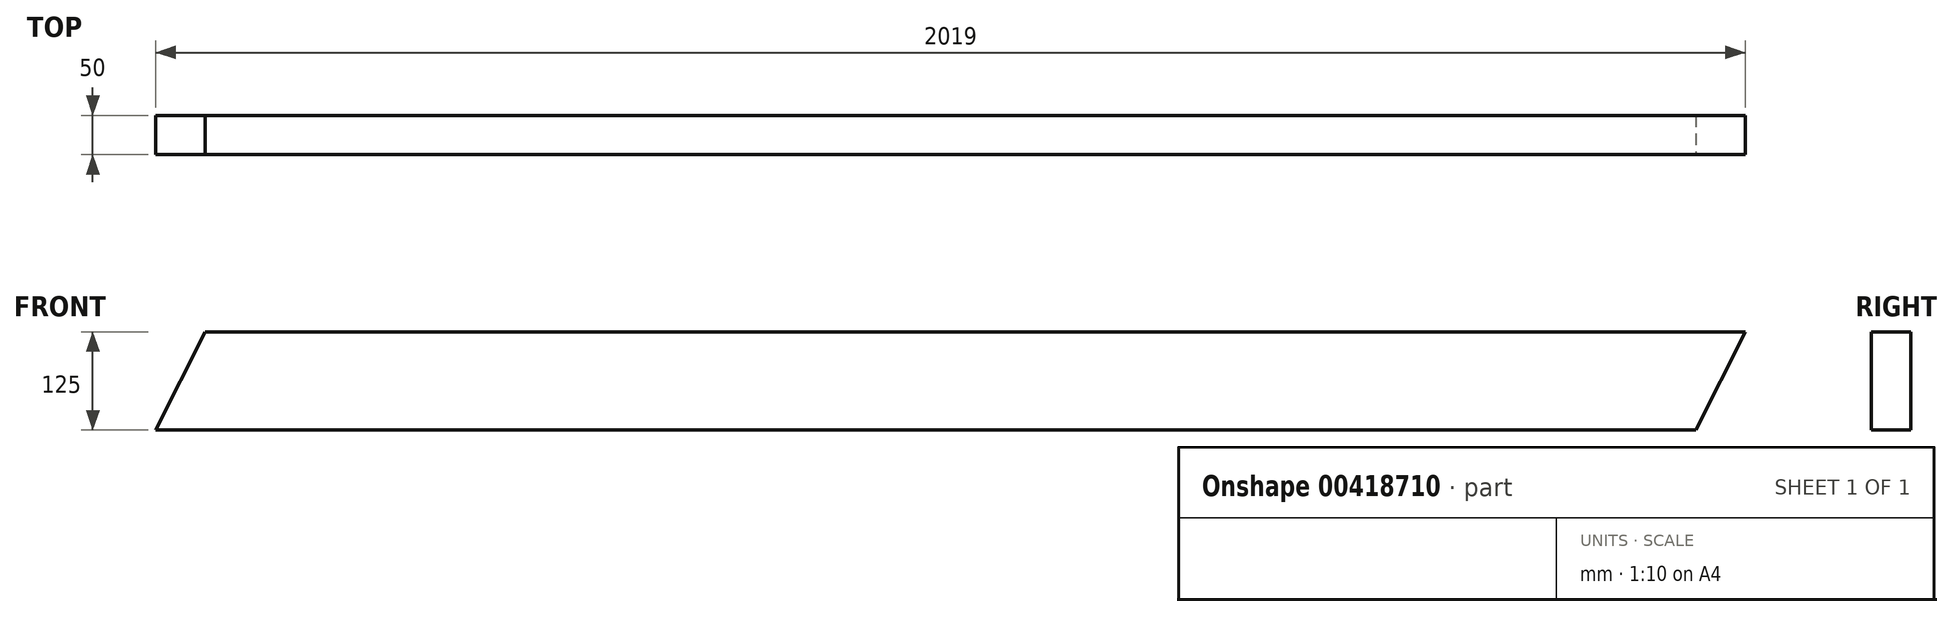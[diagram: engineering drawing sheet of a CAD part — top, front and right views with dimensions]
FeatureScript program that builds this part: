
annotation { "Feature Type Name" : "Feature", "Feature Type Description" : "" }
export const myFeature = defineFeature(function(context is Context, id is Id, definition is map)
    precondition{}
    {
        {
            var Q0;
            Q0=qCreatedBy(makeId("Right.planeOp"),FACE);
            var sketch = newSketch(context, id + "F0", { "sketchPlane" : qUnion([Q0])});
            skLineSegment(sketch, "E0.bottom", {"start": v(25, 62.5) * mm, "end": v(-25, 62.5) * mm});
            skLineSegment(sketch, "E0.top", {"start": v(25, -62.5) * mm, "end": v(-25, -62.5) * mm});
            skLineSegment(sketch, "E0.left", {"start": v(25, 62.5) * mm, "end": v(25, -62.5) * mm});
            skLineSegment(sketch, "E0.right", {"start": v(-25, 62.5) * mm, "end": v(-25, -62.5) * mm});
            skPoint(sketch, "E0.middle", {"position": v(0, 0) * mm});
            skSolve(sketch);
        }
        {
            var Q0;
            Q0 = qSketchRegion(id + "F0", true);
            extrude(context, id + "F1", {"entities" : qUnion([Q0]), "oppositeDirection" : true, "depth" : (2000 + 19) * mm});
        }
        {
            var Q0;
            Q0=qCreatedBy(makeId("Front.planeOp"),FACE);
            var sketch = newSketch(context, id + "F2", { "sketchPlane" : qUnion([Q0])});
            skLineSegment(sketch, "E1", {"start": v(0, 62.5) * mm, "end": v(0, -62.5) * mm});
            skLineSegment(sketch, "E2", {"start": v(0, -62.5) * mm, "end": v(-62.5, -62.5) * mm});
            skLineSegment(sketch, "E3", {"start": v(-62.5, -62.5) * mm, "end": v(0, 62.5) * mm});
            skLineSegment(sketch, "E4", {"start": v(-2019, -62.5) * mm, "end": v(-1956.5, 62.5) * mm});
            skLineSegment(sketch, "E5", {"start": v(-1956.5, 62.5) * mm, "end": v(-2019, 62.5) * mm});
            skLineSegment(sketch, "E6", {"start": v(-2019, 62.5) * mm, "end": v(-2019, -62.5) * mm});
            skSolve(sketch);
        }
        {
            var Q0;
            Q0 = qSketchRegion(id + "F2", true);
            extrude(context, id + "F3", {"entities" : qUnion([Q0]), "operationType" : NewBodyOperationType.REMOVE, "endBound" : BoundingType.UP_TO_NEXT, "oppositeDirection" : true, "depth" : 25 * mm, "hasSecondDirection" : true, "secondDirectionBound" : SecondDirectionBoundingType.UP_TO_NEXT, "secondDirectionOppositeDirection" : false, "secondDirectionDepth" : 25 * mm});
        }
    });
